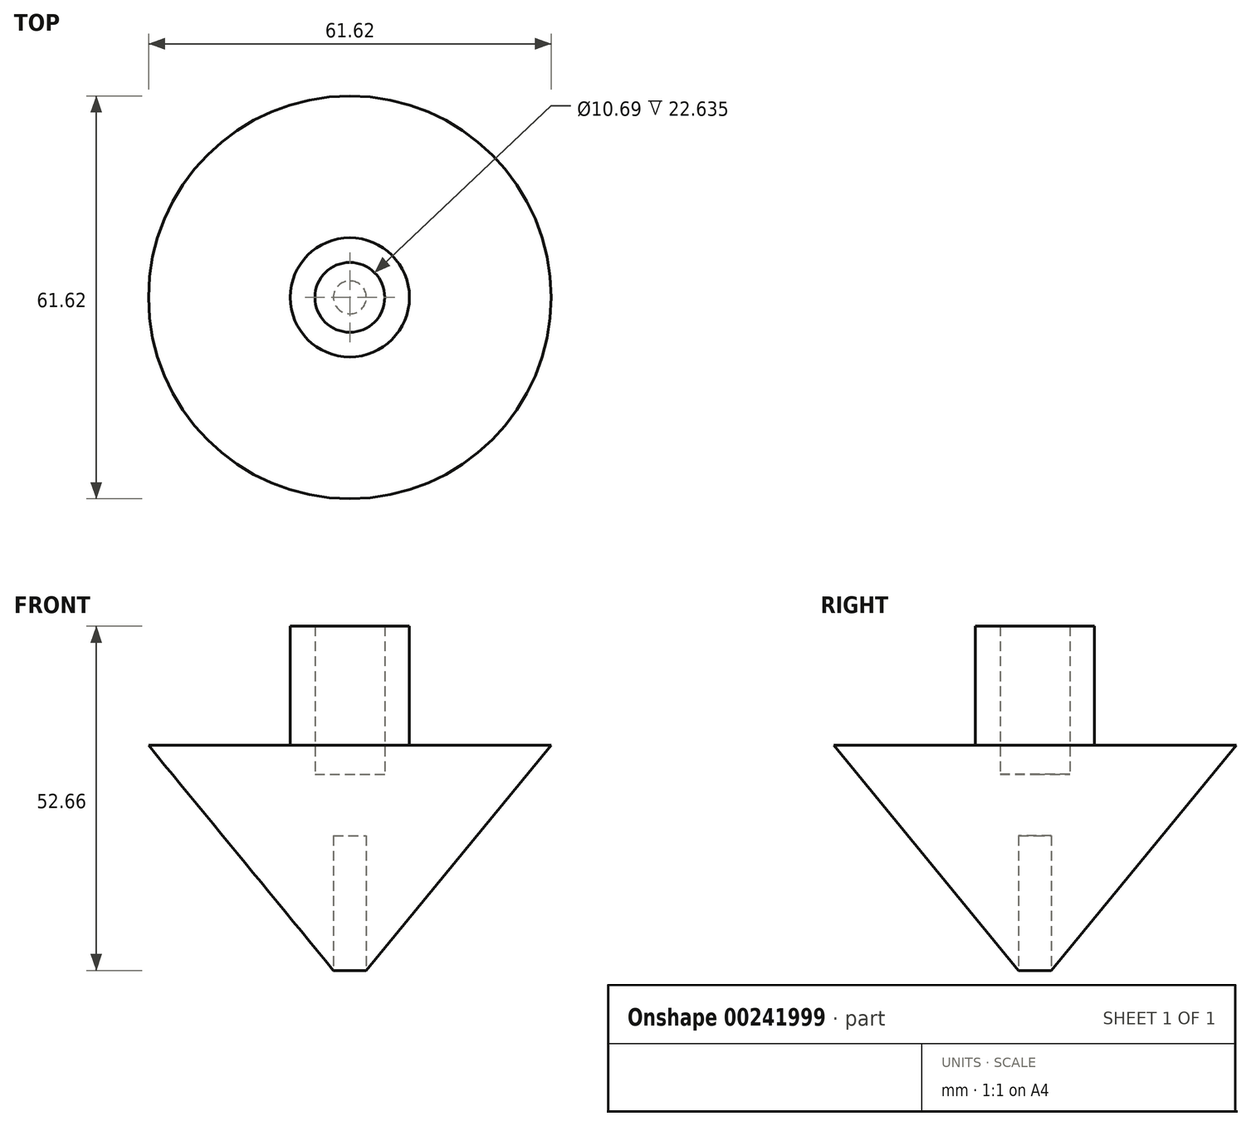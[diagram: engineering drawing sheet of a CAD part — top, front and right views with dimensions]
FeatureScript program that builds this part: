
annotation { "Feature Type Name" : "Feature", "Feature Type Description" : "" }
export const myFeature = defineFeature(function(context is Context, id is Id, definition is map)
    precondition{}
    {
        {
            var Q0;
            Q0=qCreatedBy(makeId("Front.planeOp"),FACE);
            var sketch = newSketch(context, id + "F0", { "sketchPlane" : qUnion([Q0])});
            skLineSegment(sketch, "E0", {"start": v(2.52, 0) * mm, "end": v(30.8, 34.42) * mm});
            skLineSegment(sketch, "E1", {"start": v(30.8, 34.42) * mm, "end": v(9.12, 34.42) * mm});
            skLineSegment(sketch, "E2", {"start": v(9.12, 34.42) * mm, "end": v(9.12, 52.66) * mm});
            skLineSegment(sketch, "E3", {"start": v(9.12, 52.66) * mm, "end": v(5.34, 52.66) * mm});
            skLineSegment(sketch, "E4", {"start": v(5.34, 52.66) * mm, "end": v(5.34, 30.02) * mm});
            skLineSegment(sketch, "E5", {"start": v(5.34, 30.02) * mm, "end": v(0, 30.02) * mm});
            skLineSegment(sketch, "E6", {"start": v(2.52, 0) * mm, "end": v(2.52, 20.6) * mm});
            skLineSegment(sketch, "E7", {"start": v(2.52, 20.6) * mm, "end": v(0, 20.6) * mm});
            skLineSegment(sketch, "E8", {"start": v(0, 20.6) * mm, "end": v(0, 30.02) * mm});
            skSolve(sketch);
        }
        {
            var Q0;
            Q0 = qSketchRegion(id + "F0", true);
            var Q1;
            Q1=sQuery(id+"F0.wireOp",EDGE,"E8");
            revolve(context, id + "F1", {"entities" : qUnion([Q0]), "axis" : qUnion([Q1]), "revolveType" : RevolveType.FULL});
        }
    });
